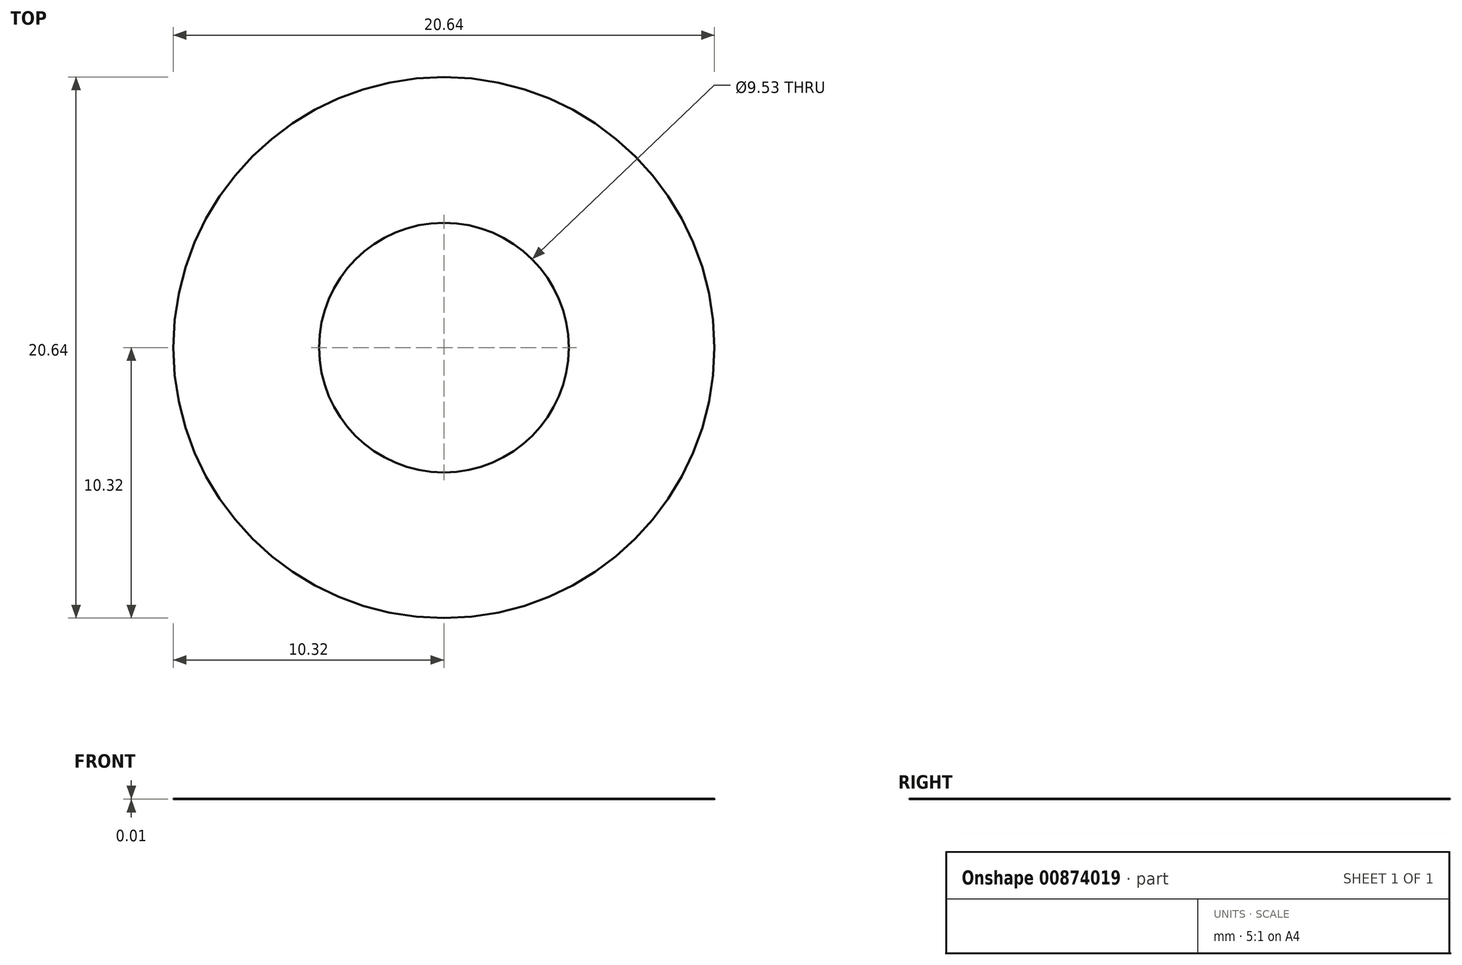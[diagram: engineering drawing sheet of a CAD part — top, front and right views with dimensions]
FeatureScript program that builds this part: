
annotation { "Feature Type Name" : "Feature", "Feature Type Description" : "" }
export const myFeature = defineFeature(function(context is Context, id is Id, definition is map)
    precondition{}
    {
        {
            var Q0;
            Q0=qCreatedBy(makeId("Top.planeOp"),FACE);
            var sketch = newSketch(context, id + "F0", { "sketchPlane" : qUnion([Q0])});
            skCircle(sketch, "E0", {"center": v(0, 0) * mm, "radius": 10.32 * mm});
            skCircle(sketch, "E1", {"center": v(0, 0) * mm, "radius": 4.76 * mm});
            skSolve(sketch);
        }
        {
            var Q0;
            Q0=makeQuery(id+"F0.imprint","IMPRINT",FACE,{"disambiguationData":[TD([[makeQuery(id+"F0.imprint","IMPRINT",EDGE,{"derivedFrom":sQuery(id+"F0.wireOp",EDGE,"E0")}),1.0]])]});
            extrude(context, id + "F1", {"entities" : qUnion([Q0]), "depth" : 5 / 406.4 * mm, "offsetDistance" : 25 * mm});
        }
    });
